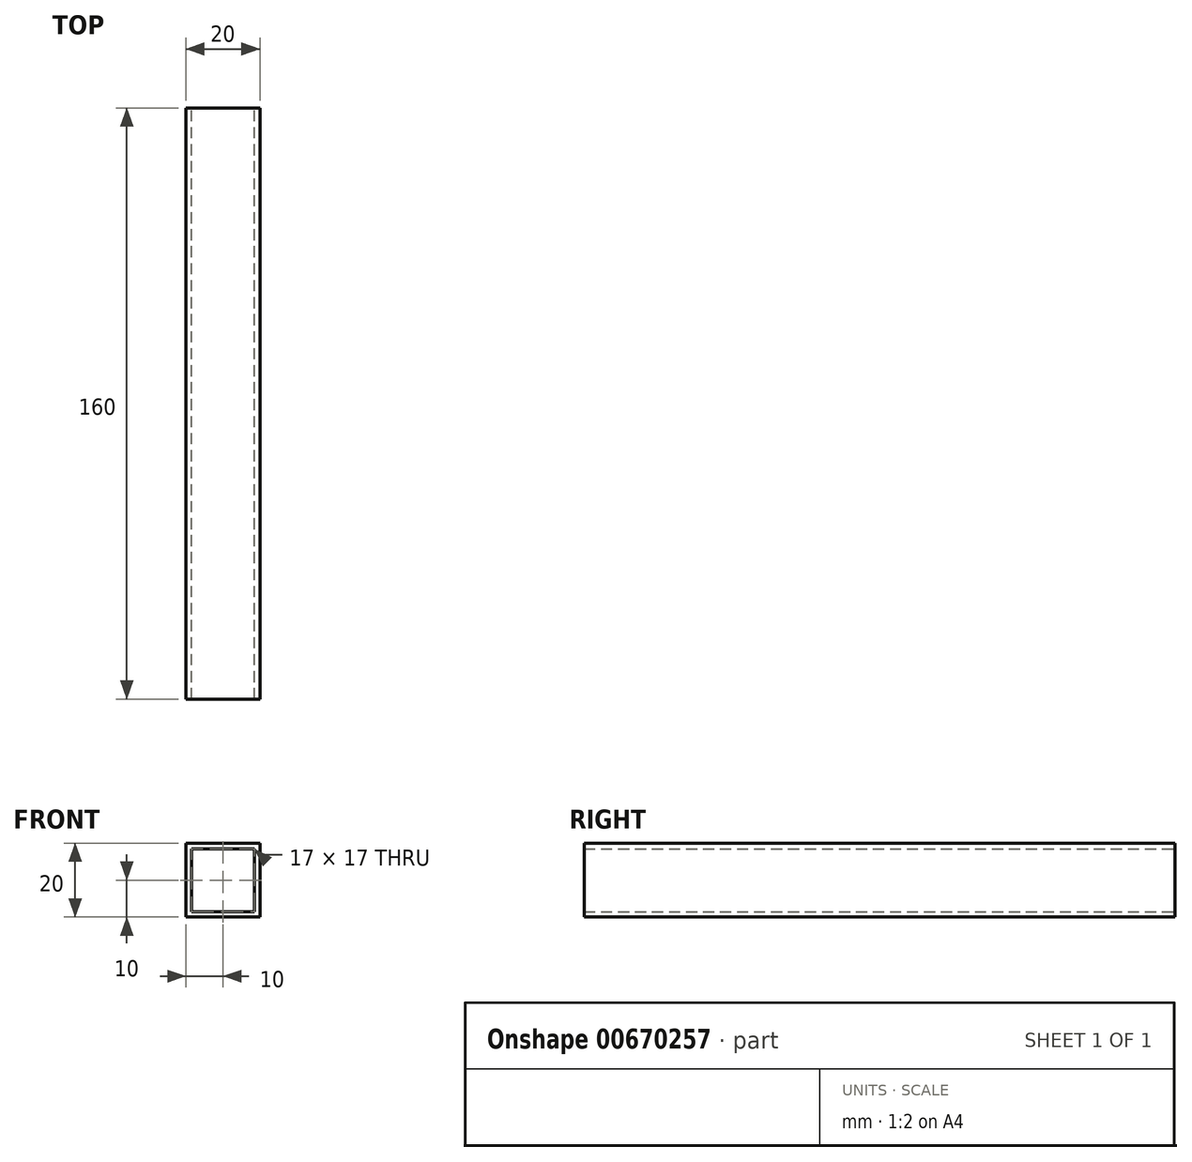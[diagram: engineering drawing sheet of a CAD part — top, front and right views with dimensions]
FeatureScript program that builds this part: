
annotation { "Feature Type Name" : "Feature", "Feature Type Description" : "" }
export const myFeature = defineFeature(function(context is Context, id is Id, definition is map)
    precondition{}
    {
        {
            var Q0;
            Q0=qCreatedBy(makeId("Front.planeOp"),FACE);
            var sketch = newSketch(context, id + "F0", { "sketchPlane" : qUnion([Q0])});
            skLineSegment(sketch, "E0.bottom", {"start": v(-10, 10) * mm, "end": v(10, 10) * mm});
            skLineSegment(sketch, "E0.top", {"start": v(-10, -10) * mm, "end": v(10, -10) * mm});
            skLineSegment(sketch, "E0.left", {"start": v(-10, 10) * mm, "end": v(-10, -10) * mm});
            skLineSegment(sketch, "E0.right", {"start": v(10, 10) * mm, "end": v(10, -10) * mm});
            skLineSegment(sketch, "E1.bottom", {"start": v(-8.5, 8.5) * mm, "end": v(8.5, 8.5) * mm});
            skLineSegment(sketch, "E1.top", {"start": v(-8.5, -8.5) * mm, "end": v(8.5, -8.5) * mm});
            skLineSegment(sketch, "E1.left", {"start": v(-8.5, 8.5) * mm, "end": v(-8.5, -8.5) * mm});
            skLineSegment(sketch, "E1.right", {"start": v(8.5, 8.5) * mm, "end": v(8.5, -8.5) * mm});
            skSolve(sketch);
        }
        {
            var Q0;
            Q0=qSketchRegion(id+"F0",true);
            extrude(context, id + "F1", {"entities" : qUnion([Q0]), "depth" : 160 * mm, "offsetDistance" : 25 * mm});
        }
    });
